# Revit family: JLG_Site_LowLevelAccess_NANOa
name_source: partatom
category: Site
revit_build: Autodesk Revit 2017 (Build: 20190508_0315(x64)
units: mm (PartAtom-declared; Revit-internal decimal feet)

## family parameters
Always vertical = Yes
Cut with Voids When Loaded = No
OmniClass Number = 23.40.00.00
OmniClass Title = Equipment and Furnishings
Part Type = Normal
Round Connector Dimension = Use Diameter
Shared = No
Work Plane-Based = No

## types (1)
- NANO
    Assembly Code = E1030100
    AssetType = Movable
    BIMObjectName = JLG_Site_LowLevelAccess_NANO
    ClassificationName = Uniclass2015
    ClassificationValue = TE_30_30_10_60
    ClosedHeight = 1.56m (5 ft 1in)
    ClosedLength = 1.195m (3 ft 11 in)
    ClosedWidth = 0.75m (2 ft  6 in)
    DocumentationCertificates = https://www.bimstore.co
    DocumentationInstallationGuide = https://www.bimstore.co
    DocumentationLiterature = https://www.bimstore.co
    DocumentationMaintenance = https://www.bimstore.co
    DocumentationTechnical = https://www.bimstore.co
    DurationUnit = Years
    ExpectedLife = 0
    IfcExportAs = IfcTransportElement
    IfcExportType = IfcTransportElementType
    Keynote = X
    MachineWeightCE = 285kg (628 lbs)
    Manufacturer = JLG
    ManufacturerName = JLG
    Material = Steel
    MaximumPlatformHeight = 2.50m (8 ft 2 in)
    MaximumWorkingHeight = 4.50m (14 ft 9 in)
    Model = Low Level Access - NANO
    ModelNumber = Low Level Access - NANO
    ModelReference = Low Level Access
    NBSDescription = Lift platforms
    NBSObjectName = JLG - Lift platforms
    NominalDepth = 0 mm  [stored 0 ft]
    NominalHeight = 0 mm  [stored 0 ft]
    NominalLength = 0 mm  [stored 0 ft]
    PlatformCapacityCE = 200 kg (441 lbs)
    PlatformSize = 1.0m x 0.73m (3 ft 3 in x 2 ft 5 in)
    PowerOptions = 12v DC Battery
    ProductionYear = 2020
    TiltAlarm = Avaliable as an option
    Type Comments = JLG_Site_LowLevelAccess_NANO
    TypeName = JLG_Site_LowLevelAccess_NANO
    URL = https://www.jlg.com
    UniqueModelReferenceFAPL = 1001252005
    WarrantyDurationLabor = 0
    WarrantyDurationParts = 0
    WarrantyDurationUnit = Years
    WarrantyGuarantorLabor = https://www.jlg.com
    WarrantyGuarantorParts = https://www.jlg.com
    WheelsAndTyres = Heavy Duty Auto-Lok on Elevation
    _BSBibleVersion = 16
    _BimSpecGuid = 0
    _CurrentRevision = 1
    _DistributedBy = https://www.bimstore.co
    _ObjectUserGuide = https://www.bimstore.co

note: [stored X ft] marks values corroborated as IEEE doubles in the binary element streams (Revit-internal decimal feet)

## geometry (parser evidence)
native form markers: Sweep x20
no freeform markers — native parametric forms only
